# Revit family: Kohler Purist 14404A-4AND-RGD Family
name_source: partatom
category: Plumbing Fixtures
revit_build: Autodesk Revit 2018 (Build: 20170223_1515(x64)
units: mm (PartAtom-declared; Revit-internal decimal feet)

## family parameters
Cut with Voids When Loaded = No
Host = Face
Part Type = Normal
Room Calculation Point = No
Round Connector Dimension = Use Diameter
Shared = No

## types (1)
- Kohler 14404A-4AND-RGD
    Default Elevation = 1219 mm
    Description = Purist Tall Single Lever Basin Mixer
    Disclamer = Although care has been taken to ensure, to the best of our knowledge, that all data and information contained herein is accurate
to the extent that it relates to either matters of fact or accepted practice at the time of issue. MDFC (Pty) Ltd assumes no responsibility for
any errors in, or misinterpretation of, such data and/ or information or any loss or damage arising from, or related to its use.
    Manufacturer = Kohler CO
    Material = Faucets
    Model = 14404A-4AND-RGD
    Telephone = 011 050 9000
    Total Height = 305 mm  [stored 1.00066 ft]
    URL = http://www.africa.kohler.com

note: [stored X ft] marks values corroborated as IEEE doubles in the binary element streams (Revit-internal decimal feet)

## geometry (parser evidence)
native form markers: Sweep x2
no freeform markers — native parametric forms only
